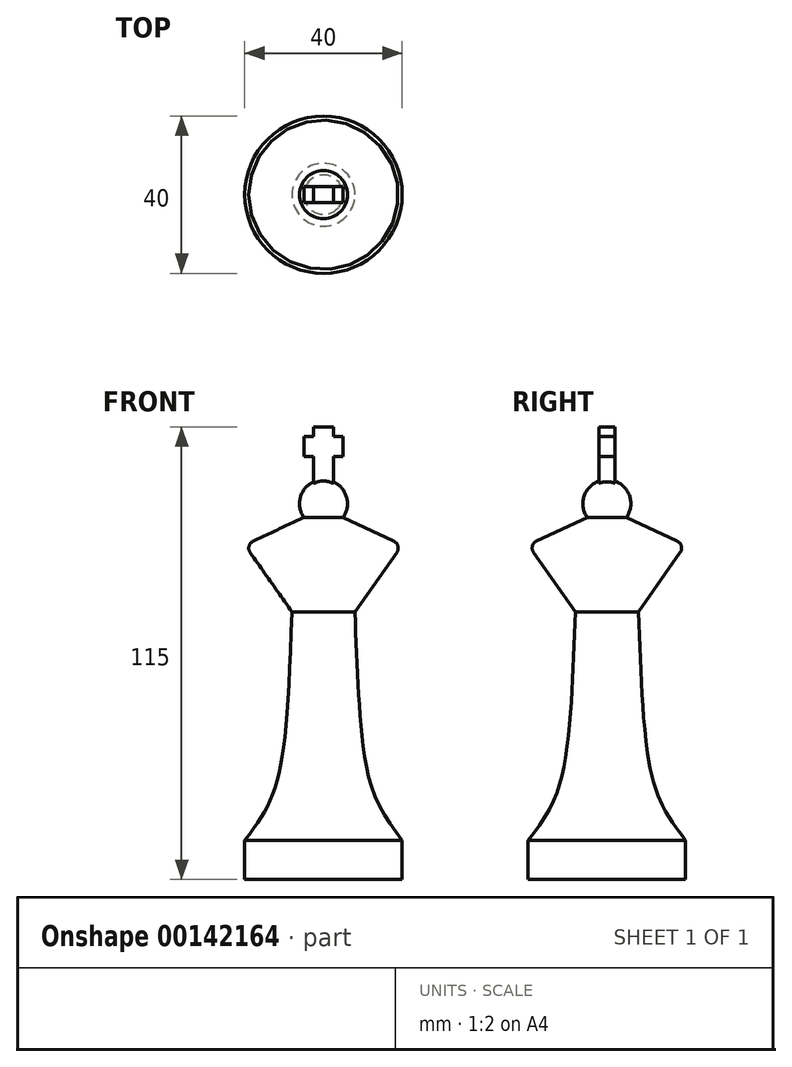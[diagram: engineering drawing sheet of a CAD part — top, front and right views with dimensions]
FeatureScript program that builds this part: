
annotation { "Feature Type Name" : "Feature", "Feature Type Description" : "" }
export const myFeature = defineFeature(function(context is Context, id is Id, definition is map)
    precondition{}
    {
        {
            var Q0;
            Q0=qCreatedBy(makeId("Front.planeOp"),FACE);
            var sketch = newSketch(context, id + "F0", { "sketchPlane" : qUnion([Q0])});
            skLineSegment(sketch, "E0.bottom", {"start": v(-2.5, 115) * mm, "end": v(2.5, 115) * mm});
            skLineSegment(sketch, "E0.top", {"start": v(-2.5, 100) * mm, "end": v(2.5, 100) * mm});
            skLineSegment(sketch, "E0.left", {"start": v(-2.5, 115) * mm, "end": v(-2.5, 100) * mm});
            skLineSegment(sketch, "E0.right", {"start": v(2.5, 115) * mm, "end": v(2.5, 100) * mm});
            skSolve(sketch);
        }
        {
            var Q0;
            Q0 = qSketchRegion(id + "F0", true);
            extrude(context, id + "F1", {"entities" : qUnion([Q0]), "depth" : 2 * mm, "hasSecondDirection" : true, "secondDirectionOppositeDirection" : true, "secondDirectionDepth" : 2 * mm});
        }
        {
            var Q0;
            Q0=makeQuery(id+"F1.opExtrude","CAP_FACE",FACE,{"disambiguationData":[OSD([sQuery(id+"F0.wireOp",EDGE,"E0.bottom"),sQuery(id+"F0.wireOp",EDGE,"E0.top"),sQuery(id+"F0.wireOp",EDGE,"E0.left"),sQuery(id+"F0.wireOp",EDGE,"E0.right")])],"isStart":false});
            var sketch = newSketch(context, id + "F2", { "sketchPlane" : qUnion([Q0])});
            skLineSegment(sketch, "E1.bottom", {"start": v(-5, 112.5) * mm, "end": v(5, 112.5) * mm});
            skLineSegment(sketch, "E1.top", {"start": v(-5, 107.5) * mm, "end": v(5, 107.5) * mm});
            skLineSegment(sketch, "E1.left", {"start": v(-5, 112.5) * mm, "end": v(-5, 107.5) * mm});
            skLineSegment(sketch, "E1.right", {"start": v(5, 112.5) * mm, "end": v(5, 107.5) * mm});
            skSolve(sketch);
        }
        {
            var Q0;
            Q0 = qSketchRegion(id + "F2", true);
            extrude(context, id + "F3", {"entities" : qUnion([Q0]), "operationType" : NewBodyOperationType.ADD, "oppositeDirection" : true, "depth" : 4 * mm});
        }
        {
            var Q0;
            Q0=qCreatedBy(makeId("Front.planeOp"),FACE);
            var sketch = newSketch(context, id + "F4", { "sketchPlane" : qUnion([Q0])});
            skLineSegment(sketch, "E2", {"start": v(-5, 92) * mm, "end": v(-20, 85) * mm});
            skLineSegment(sketch, "E3", {"start": v(-20, 85) * mm, "end": v(-8, 68) * mm});
            skLineSegment(sketch, "E4", {"start": v(0, 0) * mm, "end": v(0, 101.58) * mm});
            skLineSegment(sketch, "E5", {"start": v(0, 0) * mm, "end": v(-20, 0) * mm});
            skLineSegment(sketch, "E6", {"start": v(-20, 0) * mm, "end": v(-20, 10) * mm});
            skFitSpline(sketch, "E7", {"points": [v(-8, 68) * mm, v(-20, 10) * mm], "startDerivative": vector(-4.33, -124.02) * mm, "endDerivative": vector(-27.67, -35.33) * mm});
            skArc(sketch, "E8", {"start": v(0, 101.58) * mm, "mid": v(-5.4, 98.3) * mm, "end": v(-5, 92) * mm});
            skSolve(sketch);
        }
        {
            var Q0;
            Q0=makeQuery(id+"F4.imprint","IMPRINT",FACE,{"disambiguationData":[TD([[makeQuery(id+"F4.imprint","IMPRINT",EDGE,{"derivedFrom":sQuery(id+"F4.wireOp",EDGE,"E2")}),1.0]])]});
            var Q1;
            Q1=sQuery(id+"F4.wireOp",EDGE,"E4");
            revolve(context, id + "F5", {"operationType" : NewBodyOperationType.ADD, "entities" : qUnion([Q0]), "axis" : qUnion([Q1]), "revolveType" : RevolveType.FULL});
        }
        {
            var Q0;
            Q0=makeQuery(id+"F5.opRevolve","SWEPT_EDGE",EDGE,{"disambiguationData":[OSD([sQuery(id+"F4.wireOp",EDGE,"E2"),sQuery(id+"F4.wireOp",EDGE,"E3")])]});
            fillet(context, id + "F6", {"entities" : qUnion([Q0]), "radius" : 2 * mm, "tangentPropagation" : true, "allowEdgeOverflow" : false});
        }
    });
